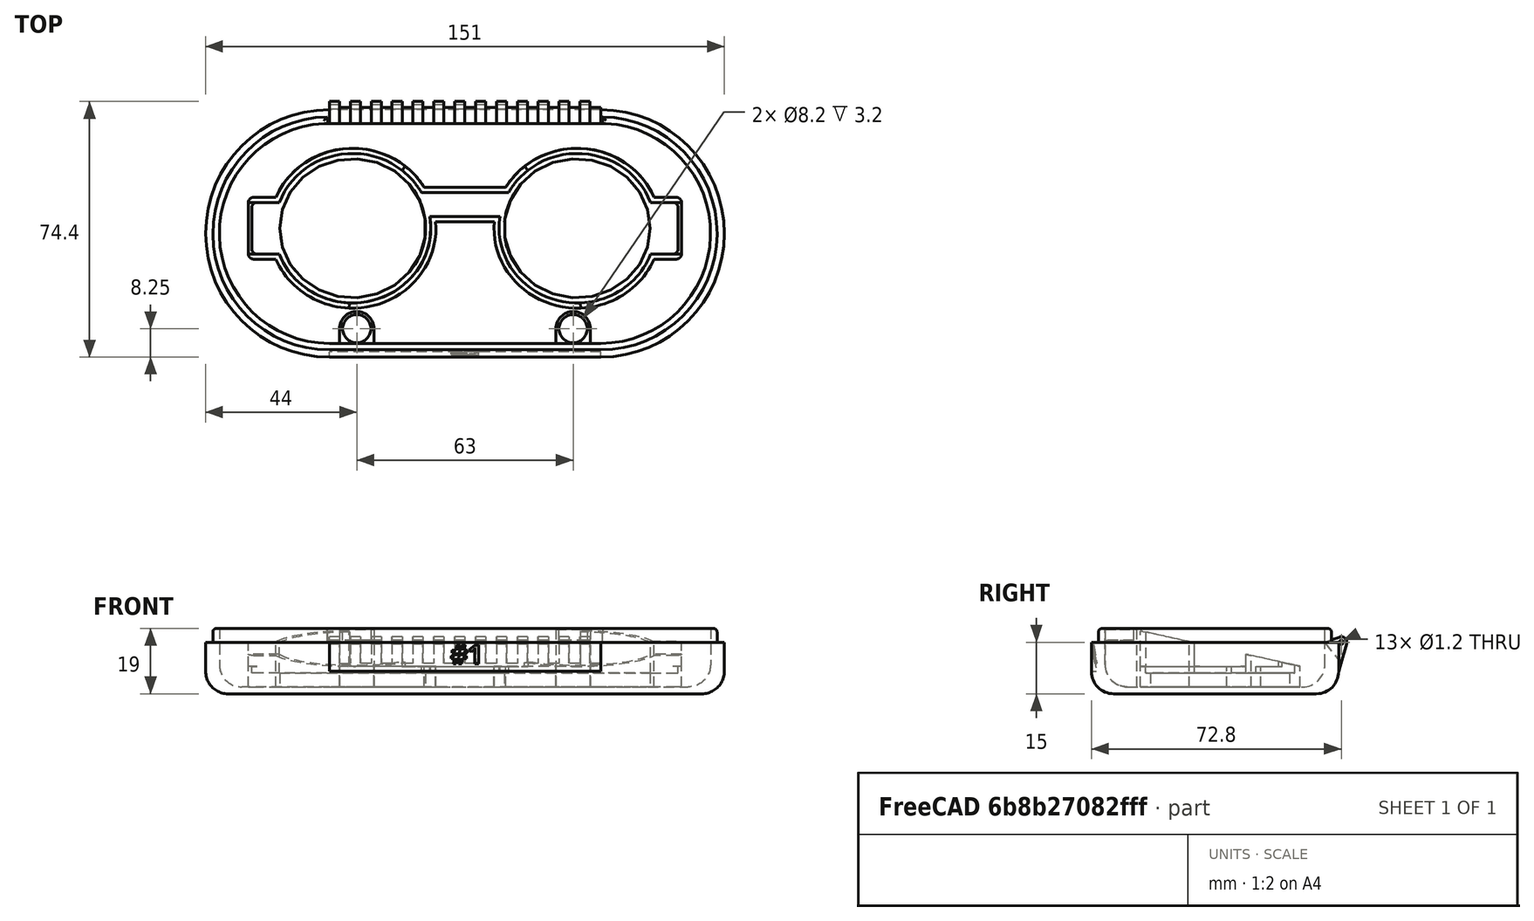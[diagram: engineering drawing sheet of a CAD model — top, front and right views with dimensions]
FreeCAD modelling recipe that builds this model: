
FCSTD DOCUMENT  (FreeCAD 1.1R39673 (Git))
Label: case_bottom
License: All rights reserved
LicenseURL: http://en.wikipedia.org/wiki/All_rights_reserved
objects: Sketcher::SketchObject×16, PartDesign::Pad×6, PartDesign::Pocket×6, PartDesign::AdditivePipe×2, PartDesign::SubtractivePipe×2, Mesh::Feature×1, PartDesign::Plane×1, PartDesign::Fillet×1, PartDesign::Mirrored×1, App::Point×1, Part::Part2DObjectPython×1, PartDesign::Body×1
note: 88 computed .brp shape members not serialized (recipe doc carries the construction recipe); baked Part::Feature solids carry a one-line shape summary decoded from their .brp

FEATURE [Sketcher::SketchObject] Sketch  label="Frame front face"
  ArcFitTolerance = 1e-06
  AttachmentSupport = -> [XY_Plane]
  ExternalTypes = [0]
  FullyConstrained = true
  MakeInternals = false
  MapMode = 5
  sketch-geometry (24):
    g0: Ellipse CenterX=-32.7 CenterY=0 CenterZ=0 NormalX=0 NormalY=0 NormalZ=1 MajorRadius=20 MinorRadius=19 AngleXU=0
    g1: LineSegment [constr] StartX=-12.7 StartY=0 StartZ=0 EndX=-52.7 EndY=0 EndZ=0
    g2: LineSegment [constr] StartX=-32.7 StartY=19 StartZ=0 EndX=-32.7 EndY=-19 EndZ=0
    g3: GeomPoint [constr] X=-26.455 Y=0 Z=0
    g4: GeomPoint [constr] X=-38.945 Y=0 Z=0
    g5: Ellipse CenterX=32.7 CenterY=0 CenterZ=0 NormalX=0 NormalY=0 NormalZ=1 MajorRadius=20 MinorRadius=19 AngleXU=0
    g6: LineSegment [constr] StartX=52.7 StartY=0 StartZ=0 EndX=12.7 EndY=0 EndZ=0
    g7: LineSegment [constr] StartX=32.7 StartY=19 StartZ=0 EndX=32.7 EndY=-19 EndZ=0
    g8: GeomPoint [constr] X=38.945 Y=0 Z=0
    g9: GeomPoint [constr] X=26.455 Y=0 Z=0
    g10: ArcOfEllipse CenterX=-32.7 CenterY=0 CenterZ=0 NormalX=0 NormalY=0 NormalZ=1 MajorRadius=22 MinorRadius=21 AngleXU=0 StartAngle=0.410218 EndAngle=6.59162
    g11: LineSegment [constr] StartX=-10.7 StartY=0 StartZ=0 EndX=-54.7 EndY=0 EndZ=0
    g12: LineSegment [constr] StartX=-32.7 StartY=21 StartZ=0 EndX=-32.7 EndY=-21 EndZ=0
    g13: GeomPoint [constr] X=-26.1426 Y=0 Z=0
    g14: GeomPoint [constr] X=-39.2574 Y=0 Z=0
    g15: ArcOfEllipse CenterX=32.7 CenterY=0 CenterZ=0 NormalX=0 NormalY=0 NormalZ=1 MajorRadius=22 MinorRadius=21 AngleXU=0 StartAngle=2.83315 EndAngle=9.01456
    g16: LineSegment [constr] StartX=54.7 StartY=0 StartZ=0 EndX=10.7 EndY=0 EndZ=0
    g17: LineSegment [constr] StartX=32.7 StartY=21 StartZ=0 EndX=32.7 EndY=-21 EndZ=0
    g18: GeomPoint [constr] X=39.2574 Y=0 Z=0
    g19: GeomPoint [constr] X=26.1426 Y=0 Z=0
    g20: LineSegment StartX=-11.7382 StartY=6.375 StartZ=0 EndX=11.7382 EndY=6.375 EndZ=0
    g21: LineSegment StartX=-12.5253 StartY=8.375 StartZ=0 EndX=12.5253 EndY=8.375 EndZ=0
    g22: Circle CenterX=-32.7 CenterY=0 CenterZ=0 NormalX=0 NormalY=0 NormalZ=1 AngleXU=0 Radius=0.5
    g23: Circle CenterX=32.7 CenterY=0 CenterZ=0 NormalX=0 NormalY=0 NormalZ=1 AngleXU=0 Radius=0.5
  constraints (33):
    c: InternalAlignment(g1-g4 -> g0) x4
    c: PointOnObject(g0,g-1)
    c: Horizontal(g1)
    c: DistanceX(g1,g1) = 40
    c: DistanceY(g2,g2) = 38
    c: InternalAlignment(g6-g9 -> g5) x4
    c: Horizontal(g6)
    c: Equal(g1,g6)
    c: Equal(g7,g2)
    c: Symmetric(g5,g0,g-2)
    c: DistanceX(g0,g5) = 65.4
    c: InternalAlignment(g11-g14 -> g10) x4
    c: Coincident(g10,g0)
    c: Horizontal(g11)
    c: DistanceX(g1,g11) = 2
    c: DistanceY(g12,g2) = 2
    c: InternalAlignment(g16-g19 -> g15) x4
    c: Symmetric(g0,g15,g-2)
    c: Horizontal(g16)
    c: Equal(g16,g11)
    c: Equal(g17,g12)
    c: Horizontal(g10,g15)
    c: Horizontal(g15,g10)
    c: Coincident(g20,g10)
    c: Coincident(g20,g15)
    c: Coincident(g21,g10)
    c: Coincident(g21,g15)
    c: Distance(g20,g21) = 2
    c: Distance(g-1,g20) = 6.375
    c: Coincident(g22,g0)
    c: Diameter(g22) = 1
    c: Equal(g22,g23)
    c: Symmetric(g22,g23,g-2)
FEATURE [Sketcher::SketchObject] Sketch001
  ArcFitTolerance = 1e-06
  AttachmentSupport = -> [XY_Plane]
  ExternalGeometry = -> [Sketch]
  ExternalTypes = [0]
  FullyConstrained = true
  MakeInternals = false
  MapMode = 5
  sketch-geometry (48):
    g0: ArcOfEllipse [constr] CenterX=-32.7 CenterY=0 CenterZ=0 NormalX=0 NormalY=0 NormalZ=1 MajorRadius=22.75 MinorRadius=21.75 AngleXU=0 StartAngle=0.497251 EndAngle=6.43899
    g1: LineSegment [constr] StartX=-9.95 StartY=0 StartZ=0 EndX=-55.45 EndY=0 EndZ=0
    g2: LineSegment [constr] StartX=-32.7 StartY=21.75 StartZ=0 EndX=-32.7 EndY=-21.75 EndZ=0
    g3: GeomPoint [constr] X=-26.0292 Y=0 Z=0
    g4: GeomPoint [constr] X=-39.3708 Y=0 Z=0
    g5: LineSegment [constr] StartX=-32.7 StartY=0 StartZ=0 EndX=-32.7 EndY=21 EndZ=0
    g6: LineSegment [constr] StartX=-32.7 StartY=0 StartZ=0 EndX=-54.7 EndY=0 EndZ=0
    g7: LineSegment StartX=-60.5594 StartY=7.5 StartZ=0 EndX=-54.0547 EndY=7.5 EndZ=0
    g8: LineSegment StartX=-60.5594 StartY=-7.5 StartZ=0 EndX=-54.0547 EndY=-7.5 EndZ=0
    g9: ArcOfEllipse CenterX=-32.7 CenterY=0 CenterZ=0 NormalX=0 NormalY=0 NormalZ=1 MajorRadius=22.75 MinorRadius=21.75 AngleXU=3.14159 StartAngle=3.63884 EndAngle=5.93113
    g10: ArcOfEllipse CenterX=-32.7 CenterY=0 CenterZ=0 NormalX=0 NormalY=0 NormalZ=1 MajorRadius=22.75 MinorRadius=21.75 AngleXU=5.5e-15 StartAngle=3.49365 EndAngle=6.43899
    g11: LineSegment StartX=-12.7051 StartY=10.375 StartZ=0 EndX=12.7051 EndY=10.375 EndZ=0
    g12: LineSegment StartX=-10.2256 StartY=3.375 StartZ=0 EndX=10.2256 EndY=3.375 EndZ=0
    g13: ArcOfEllipse [constr] CenterX=-32.7 CenterY=0 CenterZ=0 NormalX=0 NormalY=0 NormalZ=1 MajorRadius=24.25 MinorRadius=23.25 AngleXU=0 StartAngle=0.53606 EndAngle=6.36392
    g14: LineSegment [constr] StartX=-8.45 StartY=0 StartZ=0 EndX=-56.95 EndY=0 EndZ=0
    g15: LineSegment [constr] StartX=-32.7 StartY=23.25 StartZ=0 EndX=-32.7 EndY=-23.25 EndZ=0
    g16: GeomPoint [constr] X=-25.808 Y=0 Z=0
    g17: GeomPoint [constr] X=-39.592 Y=0 Z=0
    g18: ArcOfEllipse CenterX=-32.7 CenterY=0 CenterZ=0 NormalX=0 NormalY=0 NormalZ=1 MajorRadius=24.25 MinorRadius=23.25 AngleXU=-3.14159 StartAngle=3.67765 EndAngle=5.8857
    g19: LineSegment StartX=-61.5594 StartY=9 StartZ=0 EndX=-55.0594 EndY=9 EndZ=0
    g20: LineSegment StartX=-61.5594 StartY=-9 StartZ=0 EndX=-55.0594 EndY=-9 EndZ=0
    g21: ArcOfEllipse CenterX=-32.7 CenterY=0 CenterZ=0 NormalX=0 NormalY=0 NormalZ=1 MajorRadius=24.25 MinorRadius=23.25 AngleXU=3.14159 StartAngle=0.397481 EndAngle=3.22233
    g22: LineSegment StartX=-11.8516 StartY=11.875 StartZ=0 EndX=11.8516 EndY=11.875 EndZ=0
    g23: LineSegment StartX=-8.52899 StartY=1.875 StartZ=0 EndX=8.52899 EndY=1.875 EndZ=0
    g24: LineSegment StartX=-62.0594 StartY=6 StartZ=0 EndX=-62.0594 EndY=-6 EndZ=0
    g25: LineSegment StartX=-63.0594 StartY=7.5 StartZ=0 EndX=-63.0594 EndY=-7.5 EndZ=0
    g26: ArcOfEllipse CenterX=32.7 CenterY=0 CenterZ=0 NormalX=0 NormalY=0 NormalZ=1 MajorRadius=24.25 MinorRadius=23.25 AngleXU=-3.14159 StartAngle=3.53907 EndAngle=5.74713
    g27: ArcOfEllipse CenterX=32.7 CenterY=0 CenterZ=0 NormalX=0 NormalY=0 NormalZ=1 MajorRadius=22.75 MinorRadius=21.75 AngleXU=-3.14159 StartAngle=3.49365 EndAngle=5.78593
    g28: ArcOfEllipse CenterX=32.7 CenterY=0 CenterZ=0 NormalX=0 NormalY=0 NormalZ=1 MajorRadius=22.75 MinorRadius=21.75 AngleXU=3.14159 StartAngle=6.12738 EndAngle=9.07272
    g29: ArcOfEllipse CenterX=32.7 CenterY=0 CenterZ=0 NormalX=0 NormalY=0 NormalZ=1 MajorRadius=24.25 MinorRadius=23.25 AngleXU=-3.14159 StartAngle=6.20245 EndAngle=9.0273
    g30: ArcOfCircle CenterX=-60.5594 CenterY=6 CenterZ=0 NormalX=0 NormalY=0 NormalZ=1 AngleXU=0 Radius=1.5 StartAngle=1.5708 EndAngle=3.14159
    g31: GeomPoint [constr] X=-62.0594 Y=7.5 Z=0
    g32: ArcOfCircle CenterX=-61.5594 CenterY=7.5 CenterZ=0 NormalX=0 NormalY=0 NormalZ=1 AngleXU=0 Radius=1.5 StartAngle=1.5708 EndAngle=3.14159
    g33: GeomPoint [constr] X=-63.0594 Y=9 Z=0
    g34: ArcOfCircle CenterX=-60.5594 CenterY=-6 CenterZ=0 NormalX=0 NormalY=0 NormalZ=1 AngleXU=0 Radius=1.5 StartAngle=3.14159 EndAngle=4.71239
    g35: GeomPoint [constr] X=-62.0594 Y=-7.5 Z=0
    g36: ArcOfCircle CenterX=-61.5594 CenterY=-7.5 CenterZ=0 NormalX=0 NormalY=0 NormalZ=1 AngleXU=0 Radius=1.5 StartAngle=3.14159 EndAngle=4.71239
    g37: GeomPoint [constr] X=-63.0594 Y=-9 Z=0
    g38: ArcOfCircle CenterX=61.5594 CenterY=7.5 CenterZ=0 NormalX=0 NormalY=0 NormalZ=1 AngleXU=0 Radius=1.5 StartAngle=2.8455e-12 EndAngle=1.5708
    g39: LineSegment StartX=61.5594 StartY=9 StartZ=0 EndX=55.0594 EndY=9 EndZ=0
    g40: LineSegment StartX=60.5594 StartY=7.5 StartZ=0 EndX=54.0547 EndY=7.5 EndZ=0
    g41: ArcOfCircle CenterX=60.5594 CenterY=6 CenterZ=0 NormalX=0 NormalY=0 NormalZ=1 AngleXU=0 Radius=1.5 StartAngle=2.8e-14 EndAngle=1.5708
    g42: LineSegment StartX=63.0594 StartY=7.5 StartZ=0 EndX=63.0594 EndY=-7.5 EndZ=0
    g43: LineSegment StartX=62.0594 StartY=6 StartZ=0 EndX=62.0594 EndY=-6 EndZ=0
    g44: ArcOfCircle CenterX=61.5594 CenterY=-7.5 CenterZ=0 NormalX=0 NormalY=0 NormalZ=1 AngleXU=0 Radius=1.5 StartAngle=4.71239 EndAngle=6.28319
    g45: ArcOfCircle CenterX=60.5594 CenterY=-6 CenterZ=0 NormalX=0 NormalY=0 NormalZ=1 AngleXU=0 Radius=1.5 StartAngle=4.71239 EndAngle=6.28319
    g46: LineSegment StartX=60.5594 StartY=-7.5 StartZ=0 EndX=54.0547 EndY=-7.5 EndZ=0
    g47: LineSegment StartX=61.5594 StartY=-9 StartZ=0 EndX=55.0594 EndY=-9 EndZ=0
  constraints (115):
    c: Coincident(g0,g-3)
    c: InternalAlignment(g1-g4 -> g0) x4
    c: Horizontal(g1)
    c: Coincident(g5,g0)
    c: PointOnObject(g5,g-3)
    c: Vertical(g5)
    c: Coincident(g6,g0)
    c: PointOnObject(g6,g-3)
    c: Horizontal(g6)
    c: DistanceX(g1,g6) = 0.75
    c: DistanceY(g5,g2) = 0.75
    c: Distance(g0,g-5) = 3
    c: Distance(g0,g-6) = 2
    c: PointOnObject(g7,g0)
    c: Horizontal(g7)
    c: Symmetric(g8,g7,g-1)
    c: Symmetric(g31,g35,g-1)
    c: Distance(g31,g8) = 15
    c: Coincident(g9,g0)
    c: Coincident(g0,g9)
    c: Equal(g0,g9)
    c: PointOnObject(g9,g7)
    c: Coincident(g10,g0)
    c: Coincident(g10,g0)
    c: Equal(g0,g10)
    c: PointOnObject(g10,g8)
    c: Symmetric(g9,g11,g-2)
    c: Symmetric(g10,g12,g-2)
    c: Coincident(g11,g0)
    c: Coincident(g12,g0)
    c: InternalAlignment(g14-g17 -> g13) x4
    c: Coincident(g13,g0)
    c: Horizontal(g14)
    c: DistanceX(g14,g1) = 1.5
    c: DistanceY(g2,g15) = 1.5
    c: Distance(g13,g11) = 1.5
    c: Distance(g13,g12) = 1.5
    c: Coincident(g18,g0)
    c: Coincident(g18,g13)
    c: Equal(g13,g18)
    c: Coincident(g19,g18)
    c: Horizontal(g19)
    c: Distance(g33,g7) = 1.5
    c: Symmetric(g20,g18,g-1)
    c: Symmetric(g33,g37,g-1)
    c: Coincident(g21,g0)
    c: Coincident(g13,g21)
    c: Equal(g13,g21)
    c: PointOnObject(g21,g20)
    c: Symmetric(g18,g22,g-2)
    c: Symmetric(g21,g23,g-2)
    c: Coincident(g22,g13)
    c: Coincident(g23,g13)
    c: Distance(g31,g25) = 1
    c: DistanceX(g37,g20) = 8
    c: Coincident(g26,g-4)
    c: Coincident(g26,g22)
    c: Equal(g26,g18)
    c: Coincident(g27,g26)
    c: Coincident(g11,g27)
    c: Equal(g27,g9)
    c: Coincident(g28,g26)
    c: Coincident(g12,g28)
    c: Equal(g28,g10)
    c: Coincident(g29,g26)
    c: Coincident(g23,g29)
    c: Equal(g29,g21)
    c: PointOnObject(g31,g7)
    c: PointOnObject(g31,g24)
    c: Tangent(g7,g30) = 1.5708
    c: Tangent(g24,g30) = -1.5708
    c: Radius(g30) = 1.5
    c: PointOnObject(g33,g19)
    c: PointOnObject(g33,g25)
    c: Tangent(g19,g32) = 1.5708
    c: Tangent(g25,g32) = -1.5708
    c: Equal(g30,g32)
    c: PointOnObject(g35,g24)
    c: PointOnObject(g35,g8)
    c: Tangent(g24,g34) = -1.5708
    c: Tangent(g8,g34) = -1.5708
    c: PointOnObject(g37,g25)
    c: PointOnObject(g37,g20)
    c: Tangent(g25,g36) = -1.5708
    c: Tangent(g20,g36) = -1.5708
    c: Equal(g36,g34)
    c: Equal(g34,g30)
    c: Symmetric(g7,g40,g-2)
    c: Symmetric(g7,g40,g-2)
    c: Symmetric(g8,g46,g-2)
    c: Symmetric(g8,g46,g-2)
    c: Symmetric(g19,g39,g-2)
    c: Symmetric(g19,g39,g-2)
    c: Symmetric(g20,g47,g-2)
    c: Symmetric(g20,g47,g-2)
    c: Symmetric(g24,g43,g-2)
    c: Symmetric(g24,g43,g-2)
    c: Symmetric(g25,g42,g-2)
    c: Symmetric(g25,g42,g-2)
    c: Equal(g30,g41)
    c: Symmetric(g30,g41,g-2)
    c: Symmetric(g30,g41,g-2)
    c: Equal(g32,g38)
    c: Symmetric(g32,g38,g-2)
    c: Symmetric(g32,g38,g-2)
    c: Equal(g34,g45)
    c: Symmetric(g34,g45,g-2)
    c: Symmetric(g34,g45,g-2)
    c: Equal(g36,g44)
    c: Symmetric(g36,g44,g-2)
    c: Symmetric(g36,g44,g-2)
    c: PointOnObject(g27,g40)
    c: PointOnObject(g26,g39)
    c: PointOnObject(g28,g46)
    c: PointOnObject(g29,g47)
FEATURE [Mesh::Feature] assembly  label="Folded glasses footprint"
  Placement = pos=(0,0,1) rot=(-1,0,0;1.5708rad)
FEATURE [PartDesign::Pad] Pad  label="Frame holder wall"
  Direction = (0,0,1)
  Length = 15
  Length2 = 4
  Profile = -> Sketch001
  ReferenceAxis = -> Sketch001 [N_Axis]
  Refine = true
  Suppressed = false
  Type = 4
FEATURE [Sketcher::SketchObject] Sketch002
  ArcFitTolerance = 1e-06
  AttachmentSupport = -> [XY_Plane]
  ExternalGeometry = -> [Sketch,Sketch001]
  ExternalTypes = [0]
  FullyConstrained = true
  MakeInternals = false
  MapMode = 5
  sketch-geometry (46):
    g0: ArcOfEllipse CenterX=-32.7 CenterY=0 CenterZ=0 NormalX=0 NormalY=0 NormalZ=1 MajorRadius=22.75 MinorRadius=21.75 AngleXU=-3.14159 StartAngle=3.63884 EndAngle=5.93113
    g1: LineSegment [constr] StartX=-55.45 StartY=0 StartZ=0 EndX=-9.95 EndY=0 EndZ=0
    g2: LineSegment [constr] StartX=-32.7 StartY=-21.75 StartZ=0 EndX=-32.7 EndY=21.75 EndZ=0
    g3: GeomPoint [constr] X=-39.3708 Y=-8e-16 Z=0
    g4: GeomPoint [constr] X=-26.0292 Y=0 Z=0
    g5: ArcOfEllipse CenterX=-32.7 CenterY=0 CenterZ=0 NormalX=0 NormalY=0 NormalZ=1 MajorRadius=22.75 MinorRadius=21.75 AngleXU=-3.14159 StartAngle=0.352055 EndAngle=3.29739
    g6: LineSegment [constr] StartX=-55.45 StartY=-2.6e-15 StartZ=0 EndX=-9.95 EndY=2.6e-15 EndZ=0
    g7: LineSegment [constr] StartX=-32.7 StartY=-21.75 StartZ=0 EndX=-32.7 EndY=21.75 EndZ=0
    g8: GeomPoint [constr] X=-39.3708 Y=-8e-16 Z=0
    g9: GeomPoint [constr] X=-26.0292 Y=8e-16 Z=0
    g10: Ellipse CenterX=-32.7 CenterY=0 CenterZ=0 NormalX=0 NormalY=0 NormalZ=1 MajorRadius=21.25 MinorRadius=20.25 AngleXU=3.14159
    g11: LineSegment [constr] StartX=-53.95 StartY=0 StartZ=0 EndX=-11.45 EndY=0 EndZ=0
    g12: LineSegment [constr] StartX=-32.7 StartY=-20.25 StartZ=0 EndX=-32.7 EndY=20.25 EndZ=0
    g13: GeomPoint [constr] X=-39.142 Y=8e-16 Z=0
    g14: GeomPoint [constr] X=-26.258 Y=0 Z=0
    g15: ArcOfEllipse CenterX=32.7 CenterY=0 CenterZ=0 NormalX=0 NormalY=0 NormalZ=1 MajorRadius=22.75 MinorRadius=21.75 AngleXU=0 StartAngle=0.352055 EndAngle=2.64434
    g16: LineSegment [constr] StartX=55.45 StartY=0 StartZ=0 EndX=9.95 EndY=0 EndZ=0
    g17: LineSegment [constr] StartX=32.7 StartY=21.75 StartZ=0 EndX=32.7 EndY=-21.75 EndZ=0
    g18: GeomPoint [constr] X=39.3708 Y=0 Z=0
    g19: GeomPoint [constr] X=26.0292 Y=0 Z=0
    g20: LineSegment [constr] StartX=-53.95 StartY=0 StartZ=0 EndX=-52.7 EndY=0 EndZ=0
    g21: LineSegment [constr] StartX=-32.7 StartY=20.25 StartZ=0 EndX=-32.7 EndY=19 EndZ=0
    g22: LineSegment StartX=-12.7051 StartY=10.375 StartZ=0 EndX=12.7051 EndY=10.375 EndZ=0
    g23: ArcOfEllipse CenterX=32.7 CenterY=0 CenterZ=0 NormalX=0 NormalY=0 NormalZ=1 MajorRadius=22.75 MinorRadius=21.75 AngleXU=3.14159 StartAngle=6.12738 EndAngle=9.07272
    g24: LineSegment [constr] StartX=9.95 StartY=0 StartZ=0 EndX=55.45 EndY=0 EndZ=0
    g25: LineSegment [constr] StartX=32.7 StartY=-21.75 StartZ=0 EndX=32.7 EndY=21.75 EndZ=0
    g26: GeomPoint [constr] X=26.0292 Y=8e-16 Z=0
    g27: GeomPoint [constr] X=39.3708 Y=0 Z=0
    g28: Ellipse CenterX=32.7 CenterY=0 CenterZ=0 NormalX=0 NormalY=0 NormalZ=1 MajorRadius=21.25 MinorRadius=20.25 AngleXU=0
    g29: LineSegment [constr] StartX=53.95 StartY=0 StartZ=0 EndX=11.45 EndY=0 EndZ=0
    g30: LineSegment [constr] StartX=32.7 StartY=20.25 StartZ=0 EndX=32.7 EndY=-20.25 EndZ=0
    g31: GeomPoint [constr] X=39.142 Y=0 Z=0
    g32: GeomPoint [constr] X=26.258 Y=0 Z=0
    g33: LineSegment [constr] StartX=52.7 StartY=0 StartZ=0 EndX=53.95 EndY=0 EndZ=0
    g34: LineSegment [constr] StartX=32.7 StartY=19 StartZ=0 EndX=32.7 EndY=20.25 EndZ=0
    g35: LineSegment StartX=-10.2256 StartY=3.375 StartZ=0 EndX=10.2256 EndY=3.375 EndZ=0
    g36: LineSegment StartX=-54.0547 StartY=7.5 StartZ=0 EndX=-60.5594 EndY=7.5 EndZ=0
    g37: LineSegment StartX=-54.0547 StartY=-7.5 StartZ=0 EndX=-60.5594 EndY=-7.5 EndZ=0
    g38: LineSegment StartX=-62.0594 StartY=6 StartZ=0 EndX=-62.0594 EndY=-6 EndZ=0
    g39: ArcOfCircle CenterX=-60.5594 CenterY=6 CenterZ=0 NormalX=0 NormalY=0 NormalZ=1 AngleXU=0 Radius=1.5 StartAngle=1.5708 EndAngle=3.14159
    g40: ArcOfCircle CenterX=-60.5594 CenterY=-6 CenterZ=0 NormalX=0 NormalY=0 NormalZ=1 AngleXU=0 Radius=1.5 StartAngle=3.14159 EndAngle=4.71239
    g41: LineSegment StartX=54.0547 StartY=-7.5 StartZ=0 EndX=60.5594 EndY=-7.5 EndZ=0
    g42: LineSegment StartX=54.0547 StartY=7.5 StartZ=0 EndX=60.5594 EndY=7.5 EndZ=0
    g43: LineSegment StartX=62.0594 StartY=6 StartZ=0 EndX=62.0594 EndY=-6 EndZ=0
    g44: ArcOfCircle CenterX=60.5594 CenterY=6 CenterZ=0 NormalX=0 NormalY=0 NormalZ=1 AngleXU=0 Radius=1.5 StartAngle=1.48396e-11 EndAngle=1.5708
    g45: ArcOfCircle CenterX=60.5594 CenterY=-6 CenterZ=0 NormalX=0 NormalY=0 NormalZ=1 AngleXU=0 Radius=1.5 StartAngle=4.71239 EndAngle=6.28319
  constraints (73):
    c: InternalAlignment(g1-g4 -> g0) x4
    c: Coincident(g0,g-7)
    c: Horizontal(g1)
    c: PointOnObject(g1,g-7)
    c: PointOnObject(g2,g-7)
    c: PointOnObject(g0,g-9)
    c: PointOnObject(g0,g-6)
    c: InternalAlignment(g6-g9 -> g5) x4
    c: Coincident(g5,g0)
    c: Coincident(g2,g7)
    c: PointOnObject(g6,g-7)
    c: PointOnObject(g5,g-10)
    c: PointOnObject(g5,g-5)
    c: InternalAlignment(g11-g14 -> g10) x4
    c: Coincident(g10,g0)
    c: Horizontal(g11)
    c: InternalAlignment(g16-g19 -> g15) x4
    c: Coincident(g15,g-8)
    c: PointOnObject(g16,g-8)
    c: Horizontal(g16)
    c: PointOnObject(g20,g10)
    c: PointOnObject(g20,g-3)
    c: PointOnObject(g20,g1)
    c: Horizontal(g20)
    c: Coincident(g21,g12)
    c: PointOnObject(g21,g-3)
    c: PointOnObject(g21,g2)
    c: PointOnObject(g17,g-8)
    c: PointOnObject(g15,g-6)
    c: Coincident(g22,g0)
    c: Coincident(g22,g15)
    c: InternalAlignment(g24-g27 -> g23) x4
    c: Coincident(g23,g15)
    c: Coincident(g24,g16)
    c: PointOnObject(g25,g-8)
    c: PointOnObject(g23,g-5)
    c: InternalAlignment(g29-g32 -> g28) x4
    c: Coincident(g28,g15)
    c: PointOnObject(g33,g-4)
    c: Coincident(g33,g29)
    c: PointOnObject(g33,g16)
    c: PointOnObject(g29,g-1)
    c: Equal(g33,g20)
    c: PointOnObject(g34,g-4)
    c: Coincident(g34,g30)
    c: PointOnObject(g34,g17)
    c: Equal(g34,g21)
    c: Coincident(g35,g5)
    c: Coincident(g35,g23)
    c: Coincident(g36,g0)
    c: Coincident(g36,g-9)
    c: Coincident(g37,g5)
    c: Coincident(g37,g-10)
    c: DistanceX(g1,g20) = 1.5
    c: DistanceY(g12,g2) = 1.5
    c: Coincident(g38,g-11)
    c: Coincident(g38,g-11)
    c: Coincident(g39,g38)
    c: Tangent(g39,g36) = -1.5708
    c: Coincident(g40,g38)
    c: Tangent(g40,g37) = 1.5708
    c: PointOnObject(g15,g-13)
    c: PointOnObject(g23,g-12)
    c: Coincident(g41,g23)
    c: Coincident(g41,g-12)
    c: Coincident(g42,g15)
    c: Coincident(g42,g-13)
    c: Coincident(g43,g-14)
    c: Coincident(g43,g-14)
    c: Coincident(g44,g43)
    c: Tangent(g44,g42) = 1.5708
    c: Coincident(g45,g43)
    c: Tangent(g45,g41) = -1.5708
FEATURE [PartDesign::Pad] Pad001  label="Frame holder bottom resting face"
  BaseFeature = -> Pad
  Direction = (0,0,1)
  Length = 10
  Length2 = 10
  Profile = -> Sketch002
  ReferenceAxis = -> Sketch002 [N_Axis]
  Refine = true
  Suppressed = false
  Type = 3
  UpToFace = -> Pad [Face33]
FEATURE [Sketcher::SketchObject] Sketch003
  ArcFitTolerance = 1e-06
  AttachmentSupport = -> [Pad001]
  ExternalTypes = [0]
  FullyConstrained = true
  MakeInternals = false
  MapMode = 5
  Placement = pos=(0,0,-4) rot=(1,0,0;3.14159rad)
  sketch-geometry (8):
    g0: ArcOfCircle CenterX=-39.5 CenterY=1.5 CenterZ=0 NormalX=0 NormalY=0 NormalZ=1 AngleXU=0 Radius=32 StartAngle=1.5708 EndAngle=4.71239
    g1: ArcOfCircle CenterX=39.5 CenterY=1.5 CenterZ=0 NormalX=0 NormalY=0 NormalZ=1 AngleXU=0 Radius=32 StartAngle=4.71239 EndAngle=7.85398
    g2: LineSegment StartX=-39.5 StartY=33.5 StartZ=0 EndX=39.5 EndY=33.5 EndZ=0
    g3: LineSegment StartX=-39.5 StartY=-30.5 StartZ=0 EndX=39.5 EndY=-30.5 EndZ=0
    g4: ArcOfCircle CenterX=-39.5 CenterY=1.5 CenterZ=0 NormalX=0 NormalY=0 NormalZ=1 AngleXU=0 Radius=36 StartAngle=1.5708 EndAngle=4.71239
    g5: ArcOfCircle CenterX=39.5 CenterY=1.5 CenterZ=0 NormalX=0 NormalY=0 NormalZ=1 AngleXU=0 Radius=36 StartAngle=4.71239 EndAngle=7.85398
    g6: LineSegment StartX=-39.5 StartY=-34.5 StartZ=0 EndX=39.5 EndY=-34.5 EndZ=0
    g7: LineSegment StartX=-39.5 StartY=37.5 StartZ=0 EndX=39.5 EndY=37.5 EndZ=0
  constraints (25):
    c: Vertical(g0,g0)
    c: Vertical(g0,g0)
    c: Symmetric(g1,g0,g-2)
    c: Vertical(g1,g1)
    c: Vertical(g1,g1)
    c: Equal(g1,g0)
    c: Coincident(g2,g0)
    c: Coincident(g2,g1)
    c: Coincident(g3,g0)
    c: Coincident(g3,g1)
    c: DistanceX(g0,g1) = 79
    c: Radius(g0) = 32
    c: Distance(g0,g-1) = 1.5
    c: Coincident(g4,g0)
    c: Vertical(g0,g4)
    c: Vertical(g0,g4)
    c: DistanceY(g0,g4) = 4
    c: Coincident(g5,g1)
    c: Vertical(g5,g1)
    c: Vertical(g1,g5)
    c: Horizontal(g5,g4)
    c: Coincident(g6,g4)
    c: Coincident(g5,g6)
    c: Coincident(g7,g4)
    c: Coincident(g5,g7)
FEATURE [Sketcher::SketchObject] Sketch004
  ArcFitTolerance = 1e-06
  AttachmentSupport = -> [YZ_Plane]
  ExternalTypes = [0]
  FullyConstrained = true
  MakeInternals = false
  MapMode = 5
  Placement = pos=(0,0,0) rot=(0.57735,0.57735,0.57735;2.0944rad)
  sketch-geometry (6):
    g0: Circle CenterX=35.3 CenterY=9 CenterZ=0 NormalX=0 NormalY=0 NormalZ=1 AngleXU=0 Radius=0.6
    g1: LineSegment [constr] StartX=34.5 StartY=9 StartZ=0 EndX=34.7 EndY=9 EndZ=0
    g2: ArcOfCircle CenterX=35.3 CenterY=9 CenterZ=0 NormalX=0 NormalY=0 NormalZ=1 AngleXU=0 Radius=1.6 StartAngle=6.00082 EndAngle=8.19382
    g3: LineSegment StartX=30.5 StartY=9 StartZ=0 EndX=34.7667 EndY=10.5085 EndZ=0
    g4: LineSegment StartX=36.8366 StartY=8.5542 StartZ=0 EndX=34.5 EndY=0.5 EndZ=0
    g5: LineSegment StartX=30.5 StartY=9 StartZ=0 EndX=34.5 EndY=0.5 EndZ=0
  constraints (14):
    c: Diameter(g0) = 1.2
    c: Horizontal(g0,g-4)
    c: Coincident(g1,g-4)
    c: PointOnObject(g1,g0)
    c: PointOnObject(g0,g1)
    c: DistanceX(g1,g1) = 0.2
    c: Coincident(g2,g0)
    c: Diameter(g2) = 3.2
    c: Coincident(g3,g-3)
    c: Coincident(g5,g3)
    c: Tangent(g2,g3) = 1.5708
    c: Tangent(g2,g4) = 1.5708
    c: Coincident(g5,g4)
    c: Coincident(g4,g-5)
FEATURE [Sketcher::SketchObject] Sketch005  label="Hinge notches cutting path"
  ArcFitTolerance = 1e-06
  AttachmentSupport = -> [YZ_Plane]
  ExternalGeometry = -> [Sketch004]
  ExternalTypes = [0]
  FullyConstrained = true
  MakeInternals = false
  MapMode = 5
  Placement = pos=(0,0,0) rot=(0.57735,0.57735,0.57735;2.0944rad)
  sketch-geometry (5):
    g0: LineSegment [constr] StartX=35.3 StartY=9 StartZ=0 EndX=35.3 EndY=0.5 EndZ=0
    g1: LineSegment [constr] StartX=33.7634 StartY=8.5542 StartZ=0 EndX=36.1 EndY=0.5 EndZ=0
    g2: LineSegment StartX=29.1405 StartY=10.5085 StartZ=0 EndX=37.1045 EndY=0.5 EndZ=0
    g3: LineSegment [constr] StartX=35.1959 StartY=2.89863 StartZ=0 EndX=33.5551 EndY=8.5542 EndZ=0
    g4: LineSegment [constr] StartX=30.5 StartY=9 StartZ=0 EndX=30.5 EndY=8.8 EndZ=0
  constraints (16):
    c: Coincident(g0,g-3)
    c: Vertical(g0)
    c: Horizontal(g-4,g0)
    c: Symmetric(g1,g-4,g0)
    c: Symmetric(g1,g-4,g0)
    c: PointOnObject(g3,g-4)
    c: Horizontal(g3,g1)
    c: Parallel(g3,g1)
    c: Distance(g1,g3) = 0.2
    c: PointOnObject(g3,g2)
    c: Coincident(g4,g-5)
    c: PointOnObject(g4,g2)
    c: Vertical(g4)
    c: DistanceY(g4,g4) = 0.2
    c: Horizontal(g-5,g2)
    c: Horizontal(g0,g2)
FEATURE [PartDesign::Plane] DatumPlane  label="Hinge notches cutting profile plane"
  AttachmentSupport = -> [Sketch005]
  Length = 174.231
  MapMode = 7
  Placement = pos=(0,29.1405,10.5085) rot=(1,0,0;0.67213rad)
  ResizeMode = 0
  Width = 112.581
FEATURE [Sketcher::SketchObject] Sketch006
  ArcFitTolerance = 1e-06
  AttachmentSupport = -> [DatumPlane]
  ExternalGeometry = -> [Sketch003]
  ExternalTypes = [0]
  FullyConstrained = true
  MakeInternals = false
  MapMode = 5
  Placement = pos=(0,29.1405,10.5085) rot=(1,0,0;0.67213rad)
  sketch-geometry (104):
    g0: LineSegment [constr] StartX=-39.5 StartY=0 StartZ=0 EndX=-36.4615 EndY=0 EndZ=0
    g1: LineSegment [constr] StartX=-36.4615 StartY=0 StartZ=0 EndX=-33.4231 EndY=0 EndZ=0
    g2: LineSegment [constr] StartX=-33.4231 StartY=0 StartZ=0 EndX=-30.3846 EndY=0 EndZ=0
    g3: LineSegment [constr] StartX=-30.3846 StartY=0 StartZ=0 EndX=-27.3462 EndY=0 EndZ=0
    g4: LineSegment [constr] StartX=-27.3462 StartY=0 StartZ=0 EndX=-24.3077 EndY=0 EndZ=0
    g5: LineSegment [constr] StartX=-24.3077 StartY=0 StartZ=0 EndX=-21.2692 EndY=0 EndZ=0
    g6: LineSegment [constr] StartX=-21.2692 StartY=0 StartZ=0 EndX=-18.2308 EndY=0 EndZ=0
    g7: LineSegment [constr] StartX=-18.2308 StartY=0 StartZ=0 EndX=-15.1923 EndY=0 EndZ=0
    g8: LineSegment [constr] StartX=-15.1923 StartY=0 StartZ=0 EndX=-12.1538 EndY=0 EndZ=0
    g9: LineSegment [constr] StartX=-12.1538 StartY=0 StartZ=0 EndX=-9.11538 EndY=0 EndZ=0
    g10: LineSegment [constr] StartX=-9.11538 StartY=0 StartZ=0 EndX=-6.07692 EndY=0 EndZ=0
    g11: LineSegment [constr] StartX=-6.07692 StartY=0 StartZ=0 EndX=-3.03846 EndY=0 EndZ=0
    g12: LineSegment [constr] StartX=-3.03846 StartY=0 StartZ=0 EndX=-7.1e-15 EndY=0 EndZ=0
    g13: LineSegment [constr] StartX=-7.1e-15 StartY=0 StartZ=0 EndX=3.03846 EndY=0 EndZ=0
    g14: LineSegment [constr] StartX=3.03846 StartY=0 StartZ=0 EndX=6.07692 EndY=0 EndZ=0
    g15: LineSegment [constr] StartX=6.07692 StartY=0 StartZ=0 EndX=9.11538 EndY=0 EndZ=0
    g16: LineSegment [constr] StartX=9.11538 StartY=0 StartZ=0 EndX=12.1538 EndY=0 EndZ=0
    g17: LineSegment [constr] StartX=12.1538 StartY=0 StartZ=0 EndX=15.1923 EndY=0 EndZ=0
    g18: LineSegment [constr] StartX=15.1923 StartY=0 StartZ=0 EndX=18.2308 EndY=0 EndZ=0
    g19: LineSegment [constr] StartX=18.2308 StartY=0 StartZ=0 EndX=21.2692 EndY=0 EndZ=0
    g20: LineSegment [constr] StartX=21.2692 StartY=0 StartZ=0 EndX=24.3077 EndY=0 EndZ=0
    g21: LineSegment [constr] StartX=24.3077 StartY=0 StartZ=0 EndX=27.3462 EndY=0 EndZ=0
    g22: LineSegment [constr] StartX=27.3462 StartY=0 StartZ=0 EndX=30.3846 EndY=0 EndZ=0
    g23: LineSegment [constr] StartX=30.3846 StartY=0 StartZ=0 EndX=33.4231 EndY=0 EndZ=0
    g24: LineSegment [constr] StartX=33.4231 StartY=0 StartZ=0 EndX=36.4615 EndY=0 EndZ=0
    g25: LineSegment [constr] StartX=36.4615 StartY=0 StartZ=0 EndX=39.5 EndY=0 EndZ=0
    g26: LineSegment StartX=-36.5115 StartY=0 StartZ=0 EndX=-36.5115 EndY=10 EndZ=0
    g27: LineSegment StartX=-36.5115 StartY=10 StartZ=0 EndX=-36.4615 EndY=10 EndZ=0
    g28: LineSegment StartX=-36.4615 StartY=10 StartZ=0 EndX=-33.4231 EndY=10 EndZ=0
    g29: LineSegment StartX=-33.4231 StartY=10 StartZ=0 EndX=-33.3731 EndY=10 EndZ=0
    g30: LineSegment StartX=-33.3731 StartY=10 StartZ=0 EndX=-33.3731 EndY=0 EndZ=0
    g31: LineSegment StartX=-36.5115 StartY=0 StartZ=0 EndX=-33.3731 EndY=0 EndZ=0
    g32: LineSegment StartX=-30.4346 StartY=0 StartZ=0 EndX=-30.4346 EndY=10 EndZ=0
    g33: LineSegment StartX=-30.4346 StartY=10 StartZ=0 EndX=-30.3846 EndY=10 EndZ=0
    g34: LineSegment StartX=-30.3846 StartY=10 StartZ=0 EndX=-27.3462 EndY=10 EndZ=0
    g35: LineSegment StartX=-27.3462 StartY=10 StartZ=0 EndX=-27.2962 EndY=10 EndZ=0
    g36: LineSegment StartX=-27.2962 StartY=10 StartZ=0 EndX=-27.2962 EndY=0 EndZ=0
    g37: LineSegment StartX=-27.2962 StartY=0 StartZ=0 EndX=-30.4346 EndY=0 EndZ=0
    g38: LineSegment StartX=-24.3577 StartY=0 StartZ=0 EndX=-24.3577 EndY=10 EndZ=0
    g39: LineSegment StartX=-24.3577 StartY=10 StartZ=0 EndX=-24.3077 EndY=10 EndZ=0
    g40: LineSegment StartX=-24.3077 StartY=10 StartZ=0 EndX=-21.2692 EndY=10 EndZ=0
    g41: LineSegment StartX=-21.2692 StartY=10 StartZ=0 EndX=-21.2192 EndY=10 EndZ=0
    g42: LineSegment StartX=-21.2192 StartY=10 StartZ=0 EndX=-21.2192 EndY=0 EndZ=0
    g43: LineSegment StartX=-21.2192 StartY=0 StartZ=0 EndX=-24.3577 EndY=0 EndZ=0
    g44: LineSegment StartX=-18.2808 StartY=0 StartZ=0 EndX=-18.2808 EndY=10 EndZ=0
    g45: LineSegment StartX=-18.2808 StartY=10 StartZ=0 EndX=-18.2308 EndY=10 EndZ=0
    g46: LineSegment StartX=-18.2308 StartY=10 StartZ=0 EndX=-15.1923 EndY=10 EndZ=0
    g47: LineSegment StartX=-15.1923 StartY=10 StartZ=0 EndX=-15.1423 EndY=10 EndZ=0
    g48: LineSegment StartX=-15.1423 StartY=10 StartZ=0 EndX=-15.1423 EndY=0 EndZ=0
    g49: LineSegment StartX=-15.1423 StartY=0 StartZ=0 EndX=-18.2808 EndY=0 EndZ=0
    g50: LineSegment StartX=-12.2038 StartY=0 StartZ=0 EndX=-12.2038 EndY=10 EndZ=0
    g51: LineSegment StartX=-12.2038 StartY=10 StartZ=0 EndX=-12.1538 EndY=10 EndZ=0
    g52: LineSegment StartX=-12.1538 StartY=10 StartZ=0 EndX=-9.11538 EndY=10 EndZ=0
    g53: LineSegment StartX=-9.11538 StartY=10 StartZ=0 EndX=-9.06538 EndY=10 EndZ=0
    g54: LineSegment StartX=-9.06538 StartY=10 StartZ=0 EndX=-9.06538 EndY=0 EndZ=0
    g55: LineSegment StartX=-9.06538 StartY=0 StartZ=0 EndX=-12.2038 EndY=0 EndZ=0
    g56: LineSegment StartX=-6.12692 StartY=0 StartZ=0 EndX=-6.12692 EndY=10 EndZ=0
    g57: LineSegment StartX=-6.12692 StartY=10 StartZ=0 EndX=-6.07692 EndY=10 EndZ=0
    g58: LineSegment StartX=-6.07692 StartY=10 StartZ=0 EndX=-3.03846 EndY=10 EndZ=0
    g59: LineSegment StartX=-3.03846 StartY=10 StartZ=0 EndX=-2.98846 EndY=10 EndZ=0
    g60: LineSegment StartX=-2.98846 StartY=10 StartZ=0 EndX=-2.98846 EndY=0 EndZ=0
    g61: LineSegment StartX=-2.98846 StartY=0 StartZ=0 EndX=-6.12692 EndY=0 EndZ=0
    g62: LineSegment StartX=-0.05 StartY=0 StartZ=0 EndX=-0.05 EndY=10 EndZ=0
    g63: LineSegment StartX=-0.05 StartY=10 StartZ=0 EndX=-7.1e-15 EndY=10 EndZ=0
    g64: LineSegment StartX=-7.1e-15 StartY=10 StartZ=0 EndX=3.03846 EndY=10 EndZ=0
    g65: LineSegment StartX=3.03846 StartY=10 StartZ=0 EndX=3.08846 EndY=10 EndZ=0
    g66: LineSegment StartX=3.08846 StartY=10 StartZ=0 EndX=3.08846 EndY=0 EndZ=0
    g67: LineSegment StartX=3.08846 StartY=0 StartZ=0 EndX=-0.05 EndY=0 EndZ=0
    g68: LineSegment StartX=6.02692 StartY=0 StartZ=0 EndX=6.02692 EndY=10 EndZ=0
    g69: LineSegment StartX=6.02692 StartY=10 StartZ=0 EndX=6.07692 EndY=10 EndZ=0
    g70: LineSegment StartX=6.07692 StartY=10 StartZ=0 EndX=9.11538 EndY=10 EndZ=0
    g71: LineSegment StartX=9.11538 StartY=10 StartZ=0 EndX=9.16538 EndY=10 EndZ=0
    g72: LineSegment StartX=9.16538 StartY=10 StartZ=0 EndX=9.16538 EndY=0 EndZ=0
    g73: LineSegment StartX=9.16538 StartY=0 StartZ=0 EndX=6.02692 EndY=0 EndZ=0
    g74: LineSegment StartX=12.1038 StartY=0 StartZ=0 EndX=12.1038 EndY=10 EndZ=0
    g75: LineSegment StartX=12.1038 StartY=10 StartZ=0 EndX=12.1538 EndY=10 EndZ=0
    g76: LineSegment StartX=12.1538 StartY=10 StartZ=0 EndX=15.1923 EndY=10 EndZ=0
    g77: LineSegment StartX=15.1923 StartY=10 StartZ=0 EndX=15.2423 EndY=10 EndZ=0
    g78: LineSegment StartX=15.2423 StartY=10 StartZ=0 EndX=15.2423 EndY=0 EndZ=0
    g79: LineSegment StartX=15.2423 StartY=0 StartZ=0 EndX=12.1038 EndY=0 EndZ=0
    g80: LineSegment StartX=18.1808 StartY=0 StartZ=0 EndX=18.1808 EndY=10 EndZ=0
    g81: LineSegment StartX=18.1808 StartY=10 StartZ=0 EndX=18.2308 EndY=10 EndZ=0
    g82: LineSegment StartX=18.2308 StartY=10 StartZ=0 EndX=21.2692 EndY=10 EndZ=0
    g83: LineSegment StartX=21.2692 StartY=10 StartZ=0 EndX=21.3192 EndY=10 EndZ=0
    g84: LineSegment StartX=21.3192 StartY=10 StartZ=0 EndX=21.3192 EndY=0 EndZ=0
    g85: LineSegment StartX=21.3192 StartY=0 StartZ=0 EndX=18.1808 EndY=0 EndZ=0
    g86: LineSegment StartX=24.2577 StartY=0 StartZ=0 EndX=24.2577 EndY=10 EndZ=0
    g87: LineSegment StartX=24.2577 StartY=10 StartZ=0 EndX=24.3077 EndY=10 EndZ=0
    g88: LineSegment StartX=24.3077 StartY=10 StartZ=0 EndX=27.3462 EndY=10 EndZ=0
    g89: LineSegment StartX=27.3462 StartY=10 StartZ=0 EndX=27.3962 EndY=10 EndZ=0
    g90: LineSegment StartX=27.3962 StartY=10 StartZ=0 EndX=27.3962 EndY=0 EndZ=0
    g91: LineSegment StartX=27.3962 StartY=0 StartZ=0 EndX=24.2577 EndY=0 EndZ=0
    g92: LineSegment StartX=30.3346 StartY=0 StartZ=0 EndX=30.3346 EndY=10 EndZ=0
    g93: LineSegment StartX=30.3346 StartY=10 StartZ=0 EndX=30.3846 EndY=10 EndZ=0
    g94: LineSegment StartX=30.3846 StartY=10 StartZ=0 EndX=33.4231 EndY=10 EndZ=0
    g95: LineSegment StartX=33.4231 StartY=10 StartZ=0 EndX=33.4731 EndY=10 EndZ=0
    g96: LineSegment StartX=33.4731 StartY=10 StartZ=0 EndX=33.4731 EndY=0 EndZ=0
    g97: LineSegment StartX=33.4731 StartY=0 StartZ=0 EndX=30.3346 EndY=0 EndZ=0
    g98: LineSegment StartX=36.4115 StartY=0 StartZ=0 EndX=36.4115 EndY=10 EndZ=0
    g99: LineSegment StartX=36.4115 StartY=10 StartZ=0 EndX=36.4615 EndY=10 EndZ=0
    g100: LineSegment StartX=36.4615 StartY=10 StartZ=0 EndX=39.5 EndY=10 EndZ=0
    g101: LineSegment StartX=39.5 StartY=10 StartZ=0 EndX=39.55 EndY=10 EndZ=0
    g102: LineSegment StartX=39.55 StartY=10 StartZ=0 EndX=39.55 EndY=0 EndZ=0
    g103: LineSegment StartX=39.55 StartY=0 StartZ=0 EndX=36.4115 EndY=0 EndZ=0
  constraints (315):
    c: Horizontal(g0)
    c: Coincident(g0,g1)
    c: Horizontal(g1)
    c: Coincident(g1,g2)
    c: Horizontal(g2)
    c: Coincident(g2,g3)
    c: Horizontal(g3)
    c: Coincident(g3,g4)
    c: Horizontal(g4)
    c: Coincident(g4,g5)
    c: Horizontal(g5)
    c: Coincident(g5,g6)
    c: Horizontal(g6)
    c: Coincident(g6,g7)
    c: Horizontal(g7)
    c: Coincident(g7,g8)
    c: Horizontal(g8)
    c: Coincident(g8,g9)
    c: Horizontal(g9)
    c: Coincident(g9,g10)
    c: Horizontal(g10)
    c: Coincident(g10,g11)
    c: Horizontal(g11)
    c: Coincident(g11,g12)
    c: Horizontal(g12)
    c: Coincident(g12,g13)
    c: Horizontal(g13)
    c: Coincident(g13,g14)
    c: Horizontal(g14)
    c: Coincident(g14,g15)
    c: Horizontal(g15)
    c: Coincident(g15,g16)
    c: Horizontal(g16)
    c: Coincident(g16,g17)
    c: Horizontal(g17)
    c: Coincident(g17,g18)
    c: Horizontal(g18)
    c: Coincident(g18,g19)
    c: Horizontal(g19)
    c: Coincident(g19,g20)
    c: Horizontal(g20)
    c: Coincident(g20,g21)
    c: Horizontal(g21)
    c: Coincident(g21,g22)
    c: Horizontal(g22)
    c: Coincident(g22,g23)
    c: Horizontal(g23)
    c: Coincident(g23,g24)
    c: Horizontal(g24)
    c: Coincident(g24,g25)
    c: Horizontal(g25)
    c: Equal(g0,g1)
    c: Equal(g1,g2)
    c: Equal(g2,g3)
    c: Equal(g3,g4)
    c: Equal(g4,g5)
    c: Equal(g5,g6)
    c: Equal(g6,g7)
    c: Equal(g7,g8)
    c: Equal(g8,g9)
    c: Equal(g9,g10)
    c: Equal(g10,g11)
    c: Equal(g11,g12)
    c: Equal(g12,g13)
    c: Equal(g13,g14)
    c: Equal(g14,g15)
    c: Equal(g15,g16)
    c: Equal(g16,g17)
    c: Equal(g17,g18)
    c: Equal(g18,g19)
    c: Equal(g19,g20)
    c: Equal(g20,g21)
    c: Equal(g21,g22)
    c: Equal(g22,g23)
    c: Equal(g23,g24)
    c: Equal(g24,g25)
    c: DistanceX(g0,g0) = 3.03846
    c: PointOnObject(g0,g-1)
    c: PointOnObject(g26,g0)
    c: Vertical(g26)
    c: Coincident(g26,g27)
    c: Coincident(g27,g28)
    c: Horizontal(g28)
    c: Coincident(g28,g29)
    c: Coincident(g29,g30)
    c: PointOnObject(g30,g2)
    c: Vertical(g30)
    c: Horizontal(g27)
    c: Horizontal(g29)
    c: Vertical(g27,g0)
    c: Vertical(g28,g1)
    c: Coincident(g31,g26)
    c: Coincident(g31,g30)
    c: Equal(g27,g29)
    c: DistanceX(g27,g27) = 0.05
    c: PointOnObject(g32,g2)
    c: Vertical(g32)
    c: Coincident(g32,g33)
    c: Coincident(g33,g34)
    c: Horizontal(g34)
    c: Coincident(g34,g35)
    c: Horizontal(g35)
    c: Coincident(g35,g36)
    c: PointOnObject(g36,g4)
    c: Vertical(g36)
    c: Coincident(g36,g37)
    c: Coincident(g37,g32)
    c: Horizontal(g33)
    c: Equal(g27,g33)
    c: Equal(g33,g35)
    c: Vertical(g3,g34)
    c: Vertical(g33,g2)
    c: PointOnObject(g38,g4)
    c: Vertical(g38)
    c: Coincident(g38,g39)
    c: Coincident(g39,g40)
    c: Horizontal(g40)
    c: Coincident(g40,g41)
    c: Coincident(g41,g42)
    c: PointOnObject(g42,g6)
    c: Vertical(g42)
    c: Coincident(g42,g43)
    c: Coincident(g43,g38)
    c: Horizontal(g39)
    c: Horizontal(g41)
    c: Vertical(g39,g4)
    c: Vertical(g40,g5)
    c: Equal(g27,g39)
    c: Equal(g39,g41)
    c: PointOnObject(g44,g6)
    c: Vertical(g44)
    c: Coincident(g44,g45)
    c: Horizontal(g45)
    c: Coincident(g45,g46)
    c: Horizontal(g46)
    c: Coincident(g46,g47)
    c: Horizontal(g47)
    c: Coincident(g47,g48)
    c: PointOnObject(g48,g8)
    c: Vertical(g48)
    c: Coincident(g48,g49)
    c: Coincident(g49,g44)
    c: Vertical(g45,g6)
    c: Vertical(g46,g7)
    c: Equal(g45,g47)
    c: Equal(g47,g27)
    c: PointOnObject(g50,g8)
    c: Vertical(g50)
    c: Coincident(g50,g51)
    c: Horizontal(g51)
    c: Coincident(g51,g52)
    c: Horizontal(g52)
    c: Coincident(g52,g53)
    c: Horizontal(g53)
    c: Coincident(g53,g54)
    c: PointOnObject(g54,g10)
    c: Vertical(g54)
    c: Coincident(g54,g55)
    c: Coincident(g55,g50)
    c: Vertical(g51,g8)
    c: Vertical(g52,g9)
    c: Equal(g51,g53)
    c: Equal(g53,g27)
    c: PointOnObject(g56,g10)
    c: Vertical(g56)
    c: Coincident(g56,g57)
    c: Horizontal(g57)
    c: Coincident(g57,g58)
    c: Horizontal(g58)
    c: Coincident(g58,g59)
    c: Horizontal(g59)
    c: Coincident(g59,g60)
    c: PointOnObject(g60,g12)
    c: Vertical(g60)
    c: Coincident(g60,g61)
    c: Coincident(g61,g56)
    c: Vertical(g57,g10)
    c: Vertical(g58,g11)
    c: Equal(g57,g59)
    c: Equal(g59,g27)
    c: PointOnObject(g62,g12)
    c: Vertical(g62)
    c: Coincident(g62,g63)
    c: Horizontal(g63)
    c: Coincident(g63,g64)
    c: Horizontal(g64)
    c: Coincident(g64,g65)
    c: Horizontal(g65)
    c: Coincident(g65,g66)
    c: PointOnObject(g66,g14)
    c: Vertical(g66)
    c: Coincident(g66,g67)
    c: Coincident(g67,g62)
    c: Vertical(g63,g12)
    c: Vertical(g64,g13)
    c: Equal(g63,g65)
    c: Equal(g65,g27)
    c: PointOnObject(g68,g14)
    c: Vertical(g68)
    c: Coincident(g68,g69)
    c: Horizontal(g69)
    c: Coincident(g69,g70)
    c: Horizontal(g70)
    c: Coincident(g70,g71)
    c: Horizontal(g71)
    c: Coincident(g71,g72)
    c: PointOnObject(g72,g16)
    c: Vertical(g72)
    c: Coincident(g72,g73)
    c: Coincident(g73,g68)
    c: Vertical(g69,g14)
    c: Vertical(g70,g15)
    c: Equal(g69,g71)
    c: Equal(g71,g27)
    c: PointOnObject(g74,g16)
    c: Vertical(g74)
    c: Coincident(g74,g75)
    c: Horizontal(g75)
    c: Coincident(g75,g76)
    c: Horizontal(g76)
    c: Coincident(g76,g77)
    c: Horizontal(g77)
    c: Coincident(g77,g78)
    c: PointOnObject(g78,g18)
    c: Vertical(g78)
    c: Coincident(g78,g79)
    c: Coincident(g79,g74)
    c: Vertical(g16,g75)
    c: Vertical(g17,g76)
    c: Equal(g75,g77)
    c: Equal(g77,g27)
    c: PointOnObject(g80,g18)
    c: Vertical(g80)
    c: Coincident(g80,g81)
    c: Horizontal(g81)
    c: Coincident(g81,g82)
    c: Horizontal(g82)
    c: Coincident(g82,g83)
    c: Horizontal(g83)
    c: Coincident(g83,g84)
    c: PointOnObject(g84,g20)
    c: Vertical(g84)
    c: Coincident(g84,g85)
    c: PointOnObject(g85,g80)
    c: Horizontal(g85)
    c: Vertical(g18,g81)
    c: Vertical(g82,g19)
    c: Equal(g83,g81)
    c: Equal(g81,g27)
    c: PointOnObject(g86,g20)
    c: Vertical(g86)
    c: Coincident(g86,g87)
    c: Horizontal(g87)
    c: Coincident(g87,g88)
    c: Horizontal(g88)
    c: Coincident(g88,g89)
    c: Horizontal(g89)
    c: Coincident(g89,g90)
    c: PointOnObject(g90,g22)
    c: Vertical(g90)
    c: Coincident(g90,g91)
    c: Coincident(g91,g86)
    c: Vertical(g20,g87)
    c: Vertical(g88,g21)
    c: Equal(g89,g87)
    c: Equal(g87,g27)
    c: PointOnObject(g92,g22)
    c: Vertical(g92)
    c: Coincident(g92,g93)
    c: Horizontal(g93)
    c: Coincident(g93,g94)
    c: Horizontal(g94)
    c: Coincident(g94,g95)
    c: Horizontal(g95)
    c: Coincident(g95,g96)
    c: PointOnObject(g96,g24)
    c: Vertical(g96)
    c: Coincident(g96,g97)
    c: Coincident(g97,g92)
    c: Vertical(g93,g22)
    c: Vertical(g94,g23)
    c: Equal(g95,g93)
    c: Equal(g93,g27)
    c: PointOnObject(g98,g24)
    c: Vertical(g98)
    c: Coincident(g98,g99)
    c: Horizontal(g99)
    c: Coincident(g99,g100)
    c: Horizontal(g100)
    c: Coincident(g100,g101)
    c: Horizontal(g101)
    c: Coincident(g101,g102)
    c: PointOnObject(g102,g-1)
    c: Vertical(g102)
    c: Coincident(g102,g103)
    c: Coincident(g98,g103)
    c: Vertical(g99,g24)
    c: Vertical(g100,g25)
    c: DistanceY(g26,g26) = 10
    c: Equal(g26,g32)
    c: Equal(g32,g38)
    c: Equal(g38,g44)
    c: Equal(g44,g50)
    c: Equal(g50,g56)
    c: Equal(g56,g62)
    c: Equal(g62,g68)
    c: Equal(g68,g74)
    c: Equal(g74,g80)
    c: Equal(g80,g86)
    c: Equal(g86,g92)
    c: Equal(g92,g98)
    c: Vertical(g-3,g0)
    c: Equal(g95,g101)
    c: Equal(g95,g99)
    c: Vertical(g-3,g25)
FEATURE [Sketcher::SketchObject] Sketch009
  ArcFitTolerance = 1e-06
  AttachmentSupport = -> [YZ_Plane]
  ExternalGeometry = -> [Sketch001,Pad]
  ExternalTypes = [0]
  FullyConstrained = true
  MakeInternals = false
  MapMode = 5
  Placement = pos=(0,0,0) rot=(0.57735,0.57735,0.57735;2.0944rad)
  sketch-geometry (4):
    g0: LineSegment StartX=32.2714 StartY=0 StartZ=0 EndX=-35.3892 EndY=15 EndZ=0
    g1: LineSegment [constr] StartX=23.25 StartY=0 StartZ=0 EndX=23.25 EndY=2 EndZ=0
    g2: LineSegment StartX=-35.3892 StartY=15 StartZ=0 EndX=32.2714 EndY=15 EndZ=0
    g3: LineSegment StartX=32.2714 StartY=15 StartZ=0 EndX=32.2714 EndY=0 EndZ=0
  constraints (12):
    c: PointOnObject(g0,g-1)
    c: Coincident(g1,g-3)
    c: PointOnObject(g1,g0)
    c: Vertical(g1)
    c: Distance(g1,g1) = 2
    c: Coincident(g2,g0)
    c: Horizontal(g2)
    c: PointOnObject(g-4,g2)
    c: Coincident(g3,g2)
    c: Coincident(g3,g0)
    c: Vertical(g3)
    c: Angle(g0,g-1) = 0.218166
FEATURE [PartDesign::Pocket] Pocket001  label="Space for the folded temples"
  BaseFeature = -> Pad001
  Direction = (-1,0,0)
  Length = 5
  Length2 = 5
  Midplane = true
  Profile = -> Sketch009
  ReferenceAxis = -> Sketch009 [N_Axis]
  Suppressed = false
  Type = 1
FEATURE [Sketcher::SketchObject] Sketch010
  ArcFitTolerance = 1e-06
  AttachmentOffset = pos=(0,0,1.9) rot=(0,0,1;0rad)
  AttachmentSupport = -> [XY_Plane]
  ExternalGeometry = -> [Sketch001]
  ExternalTypes = [0]
  FullyConstrained = true
  MakeInternals = false
  MapMode = 5
  Placement = pos=(0,0,1.9) rot=(0,0,1;0rad)
  sketch-geometry (8):
    g0: LineSegment StartX=-32.7 StartY=0 StartZ=0 EndX=-33.7 EndY=-23.2302 EndZ=0
    g1: LineSegment StartX=-33.7 StartY=-23.2302 StartZ=0 EndX=-34.7 EndY=-46.4604 EndZ=0
    g2: LineSegment StartX=-32.7 StartY=0 StartZ=0 EndX=-17.351 EndY=18 EndZ=0
    g3: LineSegment StartX=32.7 StartY=0 StartZ=0 EndX=17.351 EndY=18 EndZ=0
    g4: LineSegment StartX=33.7 StartY=-23.2302 StartZ=0 EndX=34.7 EndY=-46.4604 EndZ=0
    g5: LineSegment StartX=32.7 StartY=0 StartZ=0 EndX=33.7 EndY=-23.2302 EndZ=0
    g6: LineSegment StartX=-17.351 StartY=18 StartZ=0 EndX=17.351 EndY=18 EndZ=0
    g7: LineSegment StartX=-34.7 StartY=-46.4604 StartZ=0 EndX=34.7 EndY=-46.4604 EndZ=0
  constraints (19):
    c: PointOnObject(g0,g-3)
    c: Coincident(g1,g0)
    c: Parallel(g1,g0)
    c: DistanceX(g0,g-3) = 1
    c: PointOnObject(g2,g-3)
    c: Distance(g2,g-1) = 18
    c: Equal(g0,g1)
    c: Symmetric(g0,g5,g-2)
    c: Symmetric(g0,g5,g-2)
    c: Symmetric(g1,g4,g-2)
    c: Symmetric(g1,g4,g-2)
    c: Symmetric(g2,g3,g-2)
    c: Symmetric(g2,g3,g-2)
    c: Coincident(g6,g2)
    c: Coincident(g6,g3)
    c: Coincident(g7,g1)
    c: Coincident(g7,g4)
    c: Coincident(g0,g-3)
    c: Coincident(g2,g0)
FEATURE [PartDesign::Pocket] Pocket002  label="Cutouts for the  temples and the frame holder on the case top"
  BaseFeature = -> Pocket001
  Direction = (0,0,-1)
  Length = 5
  Length2 = 5
  Profile = -> Sketch010
  ReferenceAxis = -> Sketch010 [N_Axis]
  Reversed = true
  Suppressed = false
  Type = 1
FEATURE [Sketcher::SketchObject] Sketch011
  ArcFitTolerance = 1e-06
  AttachmentSupport = -> [YZ_Plane]
  ExternalGeometry = -> [Pocket002,Sketch010]
  ExternalTypes = [0]
  FullyConstrained = true
  MakeInternals = false
  MapMode = 5
  Placement = pos=(0,0,0) rot=(0.57735,0.57735,0.57735;2.0944rad)
  sketch-geometry (4):
    g0: LineSegment StartX=-7.5 StartY=1.9 StartZ=0 EndX=-7.5 EndY=15.7342 EndZ=0
    g1: LineSegment StartX=-7.5 StartY=15.7342 StartZ=0 EndX=7.5 EndY=15.7342 EndZ=0
    g2: LineSegment StartX=-7.5 StartY=1.9 StartZ=0 EndX=7.5 EndY=1.9 EndZ=0
    g3: LineSegment StartX=7.5 StartY=1.9 StartZ=0 EndX=7.5 EndY=15.7342 EndZ=0
  constraints (11):
    c: Coincident(g1,g0)
    c: Horizontal(g1)
    c: PointOnObject(g0,g-5)
    c: Symmetric(g0,g0,g-3)
    c: Vertical(g0)
    c: Coincident(g2,g0)
    c: PointOnObject(g2,g-4)
    c: Horizontal(g2)
    c: Coincident(g3,g2)
    c: Coincident(g3,g1)
    c: Vertical(g3)
FEATURE [PartDesign::Pocket] Pocket003  label="Cutouts to protect the temple hinges' edges"
  BaseFeature = -> Pocket002
  Direction = (-1,0,0)
  Length = 5
  Length2 = 5
  Midplane = true
  Profile = -> Sketch011
  ReferenceAxis = -> Sketch011 [N_Axis]
  Suppressed = false
  Type = 1
FEATURE [PartDesign::Pad] Pad002  label="Case bottom"
  BaseFeature = -> Pocket003
  Direction = (0,0,-1)
  Length = 2
  Length2 = 10
  Profile = -> Sketch003 [Edge5,Edge6,Edge7,Edge8]
  ReferenceAxis = -> Sketch003 [N_Axis]
  Refine = true
  Suppressed = false
  Type = 0
FEATURE [PartDesign::Pad] Pad003  label="Case walls"
  BaseFeature = -> Pad002
  Direction = (0,0,-1)
  Length = 13
  Length2 = 10
  Profile = -> Sketch003
  ReferenceAxis = -> Sketch003 [N_Axis]
  Refine = true
  Reversed = true
  Suppressed = false
  Type = 0
FEATURE [PartDesign::AdditivePipe] AdditivePipe  label="Hinge base"
  AuxilleryCurvelinear = true
  AuxillerySpineTangent = false
  BaseFeature = -> Pad003
  Binormal = (0,0,0)
  Mode = 0
  Profile = -> Sketch004
  Refine = true
  Spine = -> Pad003 [Edge41]
  SpineTangent = false
  Suppressed = false
  Transformation = 0
  Transition = 0
FEATURE [PartDesign::Pocket] Pocket  label="Hinge notches"
  BaseFeature = -> AdditivePipe
  Direction = (0,0.622654,-0.782497)
  Length = 5
  Length2 = 5
  Profile = -> Sketch006
  ReferenceAxis = -> Sketch006 [N_Axis]
  Refine = true
  Suppressed = false
  Type = 1
FEATURE [Sketcher::SketchObject] Sketch007
  ArcFitTolerance = 1e-06
  AttachmentSupport = -> [Pocket]
  ExternalGeometry = -> [Sketch003]
  ExternalTypes = [0]
  FullyConstrained = true
  MakeInternals = false
  MapMode = 5
  Placement = pos=(0,0,9) rot=(0,0,1;0rad)
  sketch-geometry (11):
    g0: ArcOfCircle CenterX=-39.5 CenterY=-1.5 CenterZ=0 NormalX=0 NormalY=0 NormalZ=1 AngleXU=0 Radius=32 StartAngle=1.58642 EndAngle=4.71239
    g1: ArcOfCircle CenterX=-39.5 CenterY=-1.5 CenterZ=0 NormalX=0 NormalY=0 NormalZ=1 AngleXU=0 Radius=33.9 StartAngle=1.58642 EndAngle=4.71239
    g2: ArcOfCircle [constr] CenterX=-39.5 CenterY=-1.5 CenterZ=0 NormalX=0 NormalY=0 NormalZ=1 AngleXU=0 Radius=33.9 StartAngle=1.5708 EndAngle=1.58642
    g3: LineSegment [constr] StartX=-39.5 StartY=34.5 StartZ=0 EndX=-39.5 EndY=32.5 EndZ=0
    g4: LineSegment [constr] StartX=-39.5 StartY=30.5 StartZ=0 EndX=-39.5 EndY=32.5 EndZ=0
    g5: LineSegment StartX=-40.0297 StartY=32.3959 StartZ=0 EndX=-40 EndY=30.4961 EndZ=0
    g6: ArcOfCircle CenterX=39.5 CenterY=-1.5 CenterZ=0 NormalX=0 NormalY=0 NormalZ=1 AngleXU=0 Radius=32 StartAngle=4.71239 EndAngle=7.83836
    g7: ArcOfCircle CenterX=39.5 CenterY=-1.5 CenterZ=0 NormalX=0 NormalY=0 NormalZ=1 AngleXU=0 Radius=33.9 StartAngle=4.71239 EndAngle=7.83836
    g8: LineSegment StartX=40 StartY=30.4961 StartZ=0 EndX=40.0297 EndY=32.3959 EndZ=0
    g9: LineSegment StartX=-39.5 StartY=-33.5 StartZ=0 EndX=39.5 EndY=-33.5 EndZ=0
    g10: LineSegment StartX=-39.5 StartY=-35.4 StartZ=0 EndX=39.5 EndY=-35.4 EndZ=0
  constraints (30):
    c: PointOnObject(g0,g-3)
    c: Coincident(g-3,g0)
    c: Vertical(g0,g0)
    c: Coincident(g1,g0)
    c: Vertical(g1,g0)
    c: Coincident(g2,g0)
    c: Coincident(g2,g1)
    c: Vertical(g2,g0)
    c: Coincident(g3,g-5)
    c: Coincident(g4,g-3)
    c: Coincident(g4,g3)
    c: Equal(g3,g4)
    c: Coincident(g5,g1)
    c: Coincident(g5,g0)
    c: PointOnObject(g0,g5)
    c: Vertical(g3,g0)
    c: DistanceY(g2,g3) = 0.1
    c: Distance(g0,g4) = 0.5
    c: Coincident(g6,g-4)
    c: Symmetric(g0,g6,g-2)
    c: Vertical(g6,g6)
    c: Coincident(g7,g6)
    c: Symmetric(g7,g1,g-2)
    c: Vertical(g7,g6)
    c: Coincident(g8,g6)
    c: Coincident(g8,g7)
    c: Coincident(g0,g9)
    c: Coincident(g6,g9)
    c: Coincident(g7,g10)
    c: Coincident(g10,g1)
FEATURE [PartDesign::Pad] Pad004  label="Lip #1"
  BaseFeature = -> Pocket
  Direction = (0,0,1)
  Length = 4
  Length2 = 10
  Profile = -> Sketch007
  ReferenceAxis = -> Sketch007 [N_Axis]
  Refine = true
  Suppressed = false
  Type = 0
FEATURE [PartDesign::Fillet] Fillet001  label="Lip #2"
  Base = -> Pad004 [Edge371,Edge365,Edge369]
  BaseFeature = -> Pad004
  Radius = 1
  Refine = true
  SupportTransform = false
  Suppressed = false
  UseAllEdges = false
FEATURE [Sketcher::SketchObject] Sketch008
  ArcFitTolerance = 1e-06
  AttachmentOffset = pos=(0,0,-0.2) rot=(0,0,1;0rad)
  AttachmentSupport = -> [Fillet001]
  ExternalGeometry = -> [Sketch003]
  ExternalTypes = [0]
  FullyConstrained = true
  MakeInternals = false
  MapMode = 5
  Placement = pos=(0,0,12.8) rot=(0,0,1;0rad)
  sketch-geometry (5):
    g0: LineSegment StartX=-36.5 StartY=-33.5 StartZ=0 EndX=-36.5 EndY=-29.25 EndZ=0
    g1: LineSegment StartX=-26.5 StartY=-33.5 StartZ=0 EndX=-26.5 EndY=-29.25 EndZ=0
    g2: ArcOfCircle CenterX=-31.5 CenterY=-29.25 CenterZ=0 NormalX=0 NormalY=0 NormalZ=1 AngleXU=0 Radius=5 StartAngle=0 EndAngle=3.14159
    g3: LineSegment StartX=-36.5 StartY=-33.5 StartZ=0 EndX=-26.5 EndY=-33.5 EndZ=0
    g4: Circle [constr] CenterX=-31.5 CenterY=-29.25 CenterZ=0 NormalX=0 NormalY=0 NormalZ=1 AngleXU=0 Radius=4.25
  constraints (15):
    c: PointOnObject(g0,g-3)
    c: Vertical(g0)
    c: PointOnObject(g1,g-3)
    c: Vertical(g1)
    c: Horizontal(g0,g1)
    c: Distance(g1,g0) = 10
    c: Distance(g-3,g0) = 3
    c: Coincident(g2,g0)
    c: Coincident(g2,g1)
    c: Horizontal(g2,g0)
    c: Coincident(g3,g0)
    c: Coincident(g3,g1)
    c: Coincident(g4,g2)
    c: Diameter(g4) = 8.5
    c: Tangent(g3,g4)
FEATURE [PartDesign::Pad] Pad005  label="Magnet post #1"
  BaseFeature = -> Fillet001
  Direction = (0,0,1)
  Length = 10
  Length2 = 10
  Profile = -> Sketch008
  ReferenceAxis = -> Sketch008 [N_Axis]
  Refine = true
  Suppressed = false
  Type = 3
  UpToFace = -> Fillet001 [Face19]
  UpToShape = -> [Fillet001]
FEATURE [PartDesign::Mirrored] Mirrored  label="Magnet post #2"
  BaseFeature = -> Pad005
  MirrorPlane = -> Sketch008 [V_Axis]
  Originals = -> [Pad005]
  Refine = true
  Suppressed = false
  TransformMode = 0
FEATURE [Sketcher::SketchObject] Sketch012
  ArcFitTolerance = 1e-06
  AttachmentSupport = -> [Mirrored]
  ExternalGeometry = -> [Mirrored]
  ExternalTypes = [0]
  FullyConstrained = true
  MakeInternals = false
  MapMode = 5
  Placement = pos=(0,0,12.8) rot=(0,0,1;0rad)
  sketch-geometry (2):
    g0: Circle CenterX=-31.5 CenterY=-29.25 CenterZ=0 NormalX=0 NormalY=0 NormalZ=1 AngleXU=0 Radius=4.1
    g1: Circle CenterX=31.5 CenterY=-29.25 CenterZ=0 NormalX=0 NormalY=0 NormalZ=1 AngleXU=0 Radius=4.1
  constraints (4):
    c: Diameter(g0) = 8.2
    c: Equal(g0,g1)
    c: Symmetric(g0,g1,g-2)
    c: Coincident(g-3,g0)
FEATURE [PartDesign::Pocket] Pocket005  label="8x3 neodymium magnet holders"
  BaseFeature = -> Mirrored
  Direction = (0,0,-1)
  Length = 3.2
  Length2 = 5
  Profile = -> Sketch012
  ReferenceAxis = -> Sketch012 [N_Axis]
  Suppressed = false
  Type = 0
FEATURE [Sketcher::SketchObject] Sketch013
  ArcFitTolerance = 1e-06
  AttachmentSupport = -> [YZ_Plane]
  ExternalGeometry = -> [Sketch003]
  ExternalTypes = [0]
  FullyConstrained = true
  MakeInternals = false
  MapMode = 5
  Placement = pos=(0,0,0) rot=(0.57735,0.57735,0.57735;2.0944rad)
  sketch-geometry (3):
    g0: LineSegment StartX=-33.5 StartY=2.5 StartZ=0 EndX=-33.5 EndY=-4 EndZ=0
    g1: LineSegment StartX=-33.5 StartY=-4 StartZ=0 EndX=-27 EndY=-4 EndZ=0
    g2: ArcOfCircle CenterX=-27 CenterY=2.5 CenterZ=0 NormalX=0 NormalY=0 NormalZ=1 AngleXU=0 Radius=6.5 StartAngle=3.14159 EndAngle=4.71239
  constraints (8):
    c: Coincident(g0,g-3)
    c: Vertical(g0)
    c: Coincident(g1,g0)
    c: Horizontal(g1)
    c: Equal(g0,g1)
    c: Coincident(g0,g2)
    c: Tangent(g2,g1) = -1.5708
    c: Distance(g0,g0) = 6.5
FEATURE [PartDesign::AdditivePipe] AdditivePipe001  label="Inner case rounding"
  AuxilleryCurvelinear = true
  AuxillerySpineTangent = false
  BaseFeature = -> Pocket005
  Binormal = (0,0,0)
  Mode = 0
  Profile = -> Sketch013
  Spine = -> Sketch003 [Edge4,Edge1,Edge2,Edge3]
  SpineTangent = false
  Suppressed = false
  Transformation = 0
  Transition = 0
FEATURE [Sketcher::SketchObject] Sketch014
  ArcFitTolerance = 1e-06
  AttachmentSupport = -> [YZ_Plane]
  ExternalGeometry = -> [AdditivePipe001]
  ExternalTypes = [0]
  FullyConstrained = true
  MakeInternals = false
  MapMode = 5
  Placement = pos=(0,0,0) rot=(0.57735,0.57735,0.57735;2.0944rad)
  sketch-geometry (3):
    g0: LineSegment StartX=-37.5 StartY=0.5 StartZ=0 EndX=-37.5 EndY=-6 EndZ=0
    g1: LineSegment StartX=-37.5 StartY=-6 StartZ=0 EndX=-31 EndY=-6 EndZ=0
    g2: ArcOfCircle CenterX=-31 CenterY=0.5 CenterZ=0 NormalX=0 NormalY=0 NormalZ=1 AngleXU=0 Radius=6.5 StartAngle=3.14159 EndAngle=4.71239
  constraints (9):
    c: Vertical(g0)
    c: Coincident(g0,g1)
    c: Horizontal(g1)
    c: DistanceY(g0,g0) = 6.5
    c: Equal(g1,g0)
    c: Coincident(g1,g2)
    c: Coincident(g2,g0)
    c: Vertical(g1,g2)
    c: Coincident(g0,g-3)
FEATURE [App::Point] Origin001  label="Origin"
  Role = Origin
FEATURE [PartDesign::SubtractivePipe] SubtractivePipe  label="Outer case rounding"
  AuxilleryCurvelinear = true
  AuxillerySpineTangent = false
  BaseFeature = -> AdditivePipe001
  Binormal = (0,0,0)
  Mode = 0
  Profile = -> Sketch014
  Refine = true
  Spine = -> Sketch003 [Edge8,Edge5,Edge6,Edge7]
  SpineTangent = false
  Suppressed = false
  Transformation = 0
  Transition = 0
FEATURE [Sketcher::SketchObject] Sketch015
  ArcFitTolerance = 1e-06
  AttachmentSupport = -> [YZ_Plane]
  ExternalGeometry = -> [Sketch007,Sketch014]
  ExternalTypes = [0,0]
  FullyConstrained = true
  MakeInternals = false
  MapMode = 5
  Placement = pos=(0,0,0) rot=(0.57735,0.57735,0.57735;2.0944rad)
  sketch-geometry (3):
    g0: LineSegment StartX=-37.5 StartY=0.5 StartZ=0 EndX=-36 EndY=0.5 EndZ=0
    g1: LineSegment StartX=-37.5 StartY=9 StartZ=0 EndX=-36 EndY=0.5 EndZ=0
    g2: LineSegment StartX=-37.5 StartY=9 StartZ=0 EndX=-37.5 EndY=0.5 EndZ=0
  constraints (8):
    c: Coincident(g0,g-4)
    c: Horizontal(g0)
    c: Coincident(g1,g0)
    c: Coincident(g2,g1)
    c: Coincident(g2,g0)
    c: Vertical(g2)
    c: Horizontal(g1,g-3)
    c: DistanceX(g0,g0) = 1.5
FEATURE [PartDesign::SubtractivePipe] SubtractivePipe001  label="Thumb notch"
  AuxilleryCurvelinear = true
  AuxillerySpineTangent = false
  BaseFeature = -> SubtractivePipe
  Binormal = (0,0,0)
  Mode = 0
  Profile = -> Sketch015
  Refine = true
  Spine = -> Sketch003 [Edge8]
  SpineTangent = false
  Suppressed = false
  Transformation = 0
  Transition = 0
FEATURE [Part::Part2DObjectPython] ShapeString  # Draft 2D object (typed FeaturePython)
  AttachmentOffset = pos=(0,9.05,0) rot=(0,0,1;0rad)
  AttachmentSupport = -> [SubtractivePipe001]
  FontFile = <path>
  Fuse = false
  Justification = 7
  JustificationReference = 0
  KeepLeftMargin = false
  MakeFace = true
  MapMode = 5
  ObliqueAngle = 0
  Placement = pos=(4.949e-13,-36.3999,2.76632) rot=(1,0,0;1.74547rad)
  ScaleToSize = true
  Size = 5.5
  String = #1
  Tracking = 0
FEATURE [PartDesign::Pocket] Pocket006  label="Front marking"
  BaseFeature = -> SubtractivePipe001
  Direction = (-1.4e-14,0.984784,0.173785)
  Length = 0.5
  Length2 = 5
  Profile = -> ShapeString
  ReferenceAxis = -> ShapeString [N_Axis]
  Refine = true
  Suppressed = false
  Type = 0
FEATURE [PartDesign::Body] Body
  AllowCompound = false
  Group = -> [Sketch,Sketch001,Pad,Sketch002,Pad001,Sketch003,Sketch009,Pocket001,Sketch010,Pocket002,Sketch011,Pocket003,Pad002,Pad003,Sketch004,AdditivePipe,Sketch005,DatumPlane,Sketch006,Pocket,Sketch007,Pad004,Fillet001,Sketch008,Pad005,Mirrored,Sketch012,Pocket005,Sketch013,AdditivePipe001,Sketch014,SubtractivePipe,Sketch015,SubtractivePipe001,ShapeString,Pocket006]
  Origin = -> Origin
  Tip = -> Pocket006
note: 1 file-system path scrubbed to <path> (originals preserved in the JSON sidecar)
